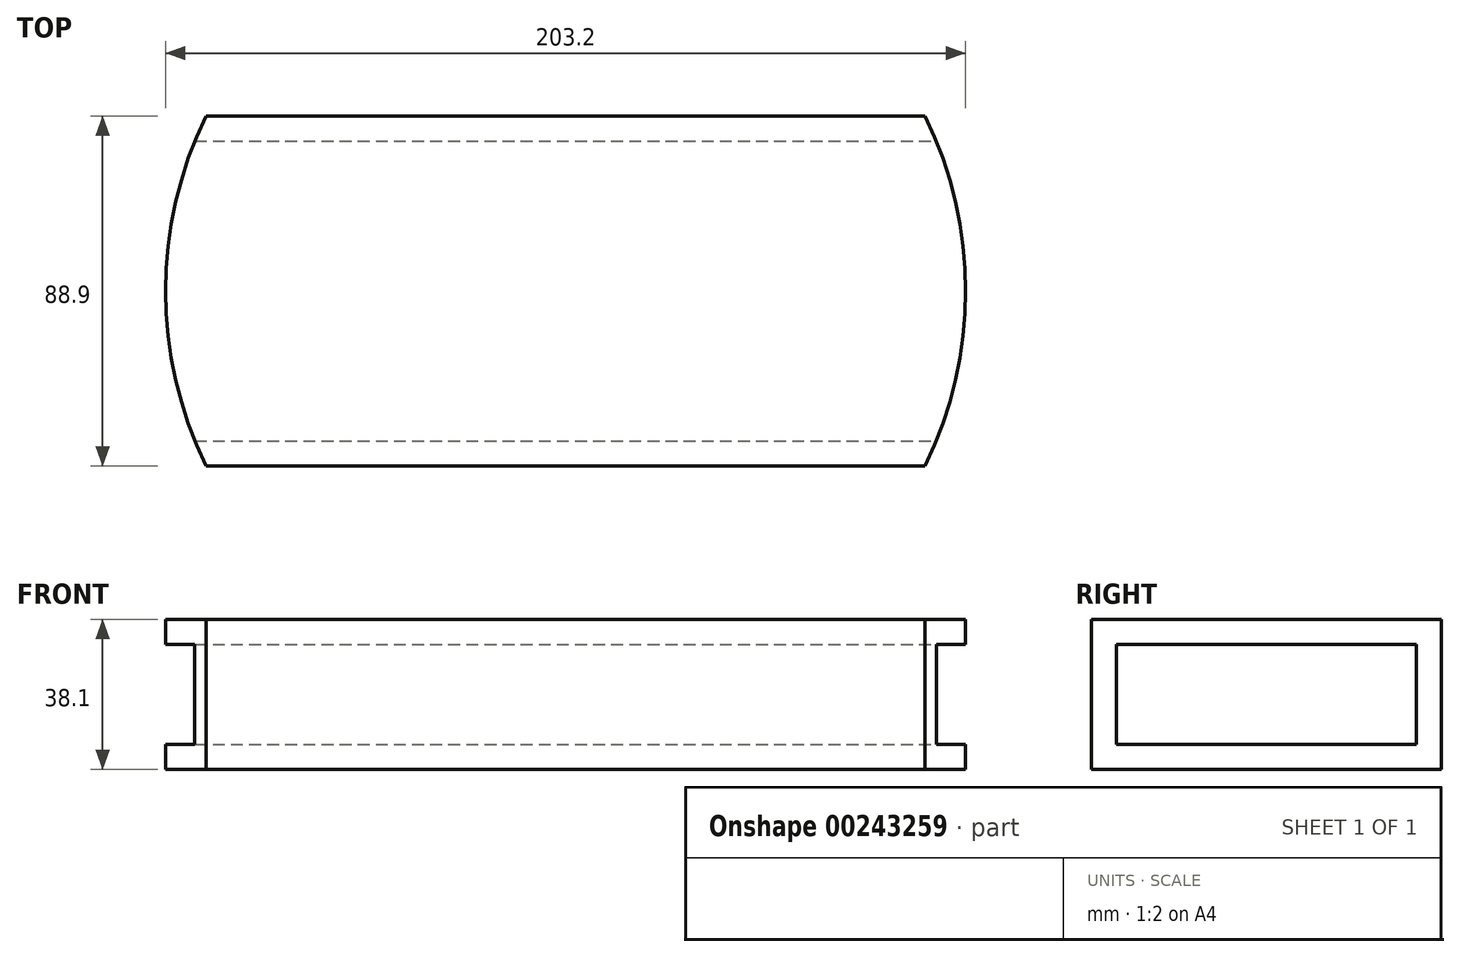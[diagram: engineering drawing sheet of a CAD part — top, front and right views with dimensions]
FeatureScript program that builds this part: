
annotation { "Feature Type Name" : "Feature", "Feature Type Description" : "" }
export const myFeature = defineFeature(function(context is Context, id is Id, definition is map)
    precondition{}
    {
        {
            var Q0;
            Q0=qCreatedBy(makeId("Top.planeOp"),FACE);
            var sketch = newSketch(context, id + "F0", { "sketchPlane" : qUnion([Q0])});
            skLineSegment(sketch, "E0", {"start": v(0, 0) * mm, "end": v(182.72, 0) * mm});
            skLineSegment(sketch, "E1", {"start": v(0, -88.9) * mm, "end": v(182.72, -88.9) * mm});
            skLineSegment(sketch, "E2", {"start": v(0, 0) * mm, "end": v(182.72, -88.9) * mm, "construction": true});
            skCircle(sketch, "E3", {"center": v(91.36, -44.45) * mm, "radius": 101.6 * mm});
            skPoint(sketch, "E4.orphan", {"position": v(182.72, 0) * mm});
            skPoint(sketch, "E5.orphan", {"position": v(0, -88.9) * mm});
            skSolve(sketch);
        }
        {
            var Q0;
            Q0=makeQuery(id+"F0.imprint","IMPRINT",FACE,{"disambiguationData":[TD([[makeQuery(id+"F0.imprint","IMPRINT",EDGE,{"derivedFrom":sQuery(id+"F0.wireOp",EDGE,"E0")}),-1.0]])]});
            extrude(context, id + "F1", {"entities" : qUnion([Q0]), "oppositeDirection" : true, "depth" : 38.1 * mm});
        }
        {
            var Q0;
            {var subQ0=sQuery(id+"F0.wireOp",EDGE,"E3");Q0=makeQuery(id+"F1.opExtrude","SWEPT_FACE",FACE,{"disambiguationData":[OSD([subQ0]),TDD([makeQuery(id+"F0.imprint","IMPRINT",EDGE,{"disambiguationData":[TD([[makeQuery(id+"F0.imprint","INTERSECT",VERTEX,{"disambiguationData":[OD(0.0)],"derivedFrom":[sQuery(id+"F0.wireOp",EDGE,"E0"),subQ0]}),-1.0]])],"derivedFrom":subQ0})])]});}
            var Q1;
            {var subQ0=sQuery(id+"F0.wireOp",EDGE,"E3");Q1=makeQuery(id+"F1.opExtrude","SWEPT_FACE",FACE,{"disambiguationData":[OSD([subQ0]),TDD([makeQuery(id+"F0.imprint","IMPRINT",EDGE,{"disambiguationData":[TD([[makeQuery(id+"F0.imprint","INTERSECT",VERTEX,{"disambiguationData":[OD(1.0)],"derivedFrom":[sQuery(id+"F0.wireOp",EDGE,"E0"),subQ0]}),1.0]])],"derivedFrom":subQ0})])]});}
            var Q2;
            Q2=makeQuery(id+"F1.opExtrude","SWEPT_BODY",BODY,{"disambiguationData":[OSD([sQuery(id+"F0.wireOp",EDGE,"E0"),sQuery(id+"F0.wireOp",EDGE,"E1"),sQuery(id+"F0.wireOp",EDGE,"sUidptVu-PXZT-9OrY-CBdE-7zYEGmsKjdn0"),sQuery(id+"F0.wireOp",EDGE,"r3Og4ldl-clYc-VgvJ-YHE6-mWevIbU6McHm")])]});
            shell(context, id + "F2", {"entities" : qUnion([Q0, Q1]), "parts" : qUnion([Q2]), "thickness" : 6.35 * mm});
        }
    });
